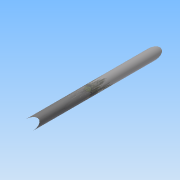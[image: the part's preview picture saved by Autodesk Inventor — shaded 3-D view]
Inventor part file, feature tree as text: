
AUTODESK INVENTOR PART (.ipt)
format: ipt  version: 2015 (Build 190159000, 159)  size: 88,576 bytes
history: native  units: mm
features: extrude x1, sketch x1
ambient origin geometry x8: Origin, YZ Plane, XZ Plane, XY Plane, X Axis, Y Axis, Z Axis, Center Point
bodies: Solid1 (feature_tree)
feature tree (2):
  extrude  "Extrusion1"  Depth=80.0mm TaperAngle=0.0deg
  sketch  "Sketch1"  dims[d0=5.0mm d1=80.0mm d2=0.0mm]
